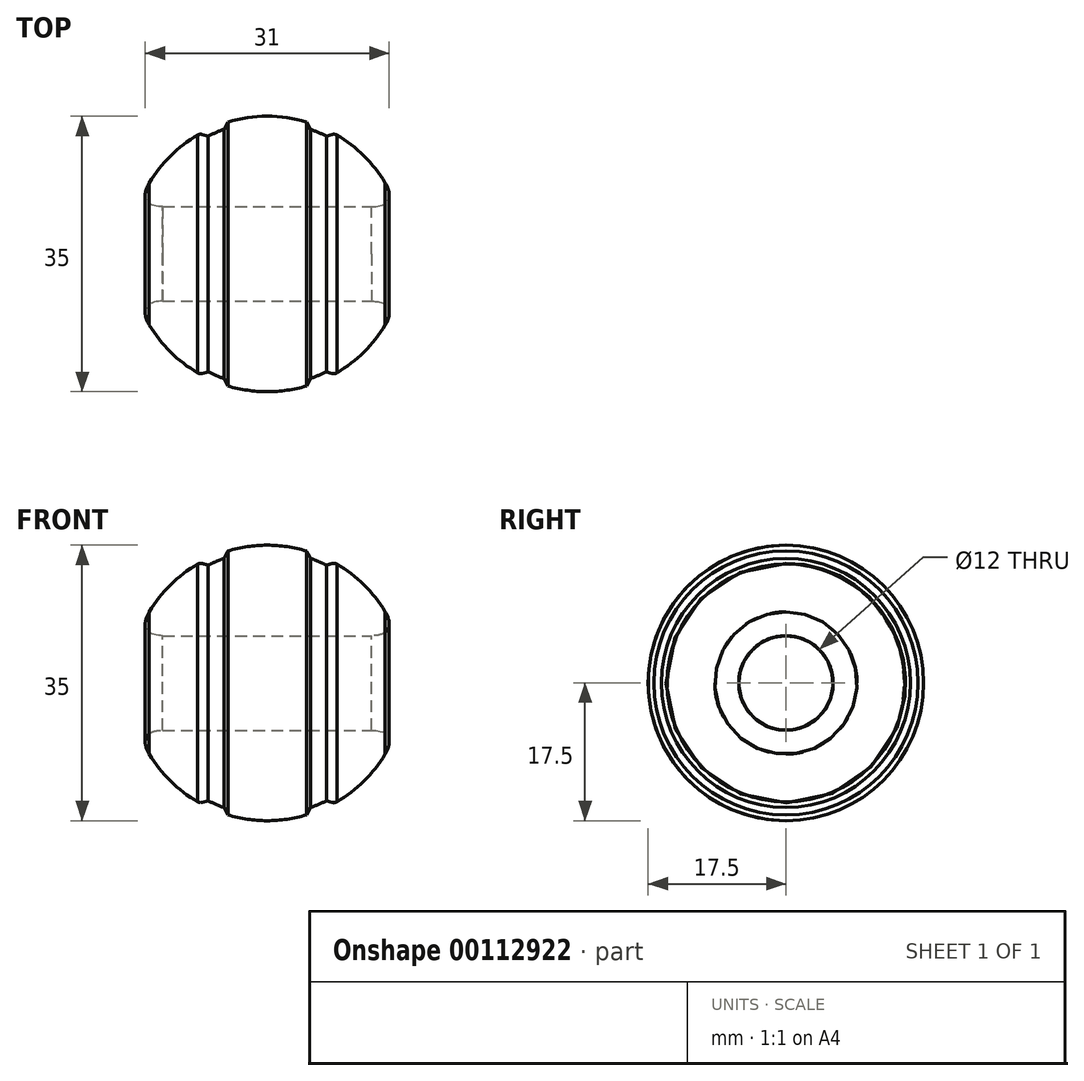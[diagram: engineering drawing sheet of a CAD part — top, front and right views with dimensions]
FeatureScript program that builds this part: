
annotation { "Feature Type Name" : "Feature", "Feature Type Description" : "" }
export const myFeature = defineFeature(function(context is Context, id is Id, definition is map)
    precondition{}
    {
        {
            var Q0;
            Q0=qCreatedBy(makeId("Front.planeOp"),FACE);
            var sketch = newSketch(context, id + "F0", { "sketchPlane" : qUnion([Q0])});
            skLineSegment(sketch, "E0", {"start": v(0, -17.5) * mm, "end": v(0, 17.5) * mm});
            skArc(sketch, "E1", {"start": v(0, 17.5) * mm, "mid": v(-17.5, 0) * mm, "end": v(0, -17.5) * mm});
            skSolve(sketch);
        }
        {
            var Q0;
            Q0=makeQuery(id+"F0.imprint","IMPRINT",FACE,{"disambiguationData":[TD([[makeQuery(id+"F0.imprint","IMPRINT",EDGE,{"derivedFrom":sQuery(id+"F0.wireOp",EDGE,"E0")}),1.0]])]});
            var Q1;
            Q1=sQuery(id+"F0.wireOp",EDGE,"E0");
            revolve(context, id + "F1", {"entities" : qUnion([Q0]), "axis" : qUnion([Q1]), "revolveType" : RevolveType.FULL});
        }
        {
            var Q0;
            Q0=qCreatedBy(makeId("Right.planeOp"),FACE);
            var sketch = newSketch(context, id + "F2", { "sketchPlane" : qUnion([Q0])});
            skCircle(sketch, "E2", {"center": v(0, 0) * mm, "radius": 6 * mm});
            skSolve(sketch);
        }
        {
            var Q0;
            Q0 = qSketchRegion(id + "F2", true);
            extrude(context, id + "F3", {"entities" : qUnion([Q0]), "operationType" : NewBodyOperationType.REMOVE, "endBound" : BoundingType.THROUGH_ALL, "oppositeDirection" : true, "depth" : 25 * mm, "hasSecondDirection" : true, "secondDirectionBound" : SecondDirectionBoundingType.THROUGH_ALL, "secondDirectionOppositeDirection" : false, "secondDirectionDepth" : 25 * mm});
        }
        {
            var Q0;
            Q0=makeQuery(id+"F3.boolean.opBoolean","COPY",FACE,{"derivedFrom":makeQuery(id+"F3.opExtrude","SWEPT_FACE",FACE,{"disambiguationData":[OSD([sQuery(id+"F2.wireOp",EDGE,"E2")])]})});
            fillet(context, id + "F4", {"entities" : qUnion([Q0]), "radius" : 2 * mm, "tangentPropagation" : true, "rho" : 0.45, "crossSection" : FilletCrossSection.CONIC, "allowEdgeOverflow" : false});
        }
        {
            var Q0;
            Q0=qCreatedBy(makeId("Front.planeOp"),FACE);
            var sketch = newSketch(context, id + "F5", { "sketchPlane" : qUnion([Q0])});
            skLineSegment(sketch, "E3", {"start": v(-8.56, 15.26) * mm, "end": v(-7.52, 14.97) * mm});
            skLineSegment(sketch, "E4", {"start": v(-5, 16.77) * mm, "end": v(-5.52, 15.82) * mm});
            skArc(sketch, "E5.0", {"start": v(-5.52, 15.82) * mm, "mid": v(-6.53, 15.42) * mm, "end": v(-7.52, 14.97) * mm});
            skLineSegment(sketch, "E6.0", {"start": v(0, -17.5) * mm, "end": v(0, 17.5) * mm, "construction": true});
            skLineSegment(sketch, "E7", {"start": v(-6.63, 14.25) * mm, "end": v(-6.63, 19.2) * mm, "construction": true});
            skLineSegment(sketch, "E8", {"start": v(-5, 16.77) * mm, "end": v(-2.72, 17.45) * mm, "construction": true});
            skLineSegment(sketch, "E9", {"start": v(-8.56, 15.26) * mm, "end": v(-10, 14.45) * mm, "construction": true});
            skArc(sketch, "E10.0", {"start": v(-5, 16.77) * mm, "mid": v(-6.82, 16.12) * mm, "end": v(-8.56, 15.26) * mm});
            skPoint(sketch, "E11.orphan", {"position": v(0, -17.5) * mm});
            skPoint(sketch, "E12.orphan", {"position": v(0, 17.5) * mm});
            skSolve(sketch);
        }
        {
            var Q0;
            Q0 = qSketchRegion(id + "F5", true);
            var Q1;
            Q1=makeQuery(id+"F3.boolean.opBoolean","COPY",FACE,{"derivedFrom":makeQuery(id+"F3.opExtrude","SWEPT_FACE",FACE,{"disambiguationData":[OSD([sQuery(id+"F2.wireOp",EDGE,"E2")])]})});
            revolve(context, id + "F6", {"entities" : qUnion([Q0]), "axis" : qUnion([Q1]), "revolveType" : RevolveType.FULL, "oppositeDirection" : true});
        }
        {
            var Q0;
            Q0=makeQuery(id+"F6.opRevolve","SWEPT_BODY",BODY,{"disambiguationData":[OSD([sQuery(id+"F5.wireOp",EDGE,"E3"),sQuery(id+"F5.wireOp",EDGE,"E4"),sQuery(id+"F5.wireOp",EDGE,"E5.0"),sQuery(id+"F5.wireOp",EDGE,"E10.0")])]});
            var Q1;
            Q1=qCreatedBy(makeId("Right.planeOp"),FACE);
            mirror(context, id + "F7", {"entities" : qUnion([Q0]), "mirrorPlane" : qUnion([Q1])});
        }
        {
            var Q0;
            Q0=makeQuery(id+"F6.opRevolve","SWEPT_BODY",BODY,{"disambiguationData":[OSD([sQuery(id+"F5.wireOp",EDGE,"E3"),sQuery(id+"F5.wireOp",EDGE,"E4"),sQuery(id+"F5.wireOp",EDGE,"E5.0"),sQuery(id+"F5.wireOp",EDGE,"E10.0")])]});
            var Q1;
            Q1=makeQuery(id+"F7.opPattern","COPY",BODY,{"derivedFrom":makeQuery(id+"F6.opRevolve","SWEPT_BODY",BODY,{"disambiguationData":[OSD([sQuery(id+"F5.wireOp",EDGE,"E3"),sQuery(id+"F5.wireOp",EDGE,"E4"),sQuery(id+"F5.wireOp",EDGE,"E5.0"),sQuery(id+"F5.wireOp",EDGE,"E10.0")])]}),"instanceName":"1"});
            var Q2;
            Q2=makeQuery(id+"F1.opRevolve","SWEPT_BODY",BODY,{"disambiguationData":[OSD([sQuery(id+"F0.wireOp",EDGE,"E0"),sQuery(id+"F0.wireOp",EDGE,"E1")])]});
            booleanBodies(context, id + "F8", {"operationType" : BooleanOperationType.SUBTRACTION, "tools" : qUnion([Q0, Q1]), "targets" : qUnion([Q2])});
        }
        {
            var Q0;
            Q0=makeQuery(id+"F8.opBoolean","COPY",EDGE,{"derivedFrom":makeQuery(id+"F6.opRevolve","SWEPT_EDGE",EDGE,{"disambiguationData":[OSD([sQuery(id+"F5.wireOp",EDGE,"E3"),sQuery(id+"F5.wireOp",EDGE,"E10.0")])]})});
            var Q1;
            Q1=makeQuery(id+"F8.opBoolean","COPY",EDGE,{"derivedFrom":makeQuery(id+"F6.opRevolve","SWEPT_EDGE",EDGE,{"disambiguationData":[OSD([sQuery(id+"F5.wireOp",EDGE,"E4"),sQuery(id+"F5.wireOp",EDGE,"E10.0")])]})});
            var Q2;
            Q2=makeQuery(id+"F8.opBoolean","COPY",EDGE,{"derivedFrom":makeQuery(id+"F7.opPattern","COPY",EDGE,{"derivedFrom":makeQuery(id+"F6.opRevolve","SWEPT_EDGE",EDGE,{"disambiguationData":[OSD([sQuery(id+"F5.wireOp",EDGE,"E4"),sQuery(id+"F5.wireOp",EDGE,"E10.0")])]}),"instanceName":"1"})});
            var Q3;
            Q3=makeQuery(id+"F8.opBoolean","COPY",EDGE,{"derivedFrom":makeQuery(id+"F7.opPattern","COPY",EDGE,{"derivedFrom":makeQuery(id+"F6.opRevolve","SWEPT_EDGE",EDGE,{"disambiguationData":[OSD([sQuery(id+"F5.wireOp",EDGE,"E3"),sQuery(id+"F5.wireOp",EDGE,"E10.0")])]}),"instanceName":"1"})});
            fillet(context, id + "F9", {"entities" : qUnion([Q0, Q1, Q2, Q3]), "radius" : 0.75 * mm, "tangentPropagation" : true, "allowEdgeOverflow" : false});
        }
    });
